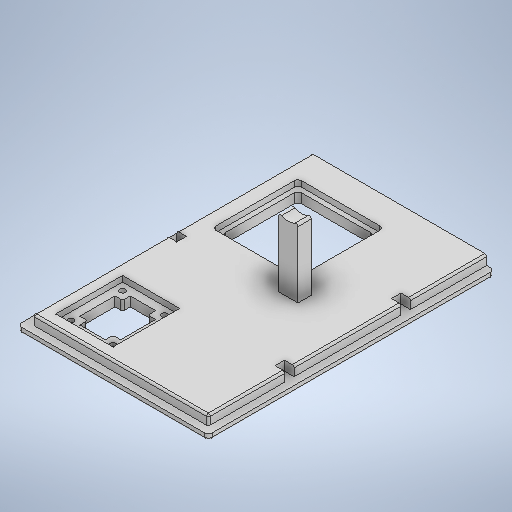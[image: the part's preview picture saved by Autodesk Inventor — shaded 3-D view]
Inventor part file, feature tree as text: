
AUTODESK INVENTOR PART (.ipt)
format: ipt  version: 2025 (Build 290162000, 162)  size: 964,608 bytes
history: native  units: mm
features: extrude x8, sketch x7, fillet x5, other x2
ambient origin geometry x8: Origin, YZ Plane, XZ Plane, XY Plane, X Axis, Y Axis, Z Axis, Center Point
bodies: Body1 (feature_tree)
feature tree (22):
  other  "ソリッド1"
  extrude  "底面"  Depth=100.0mm
  extrude  "溝"  Depth=150.0mm
  extrude  "支柱"  Depth=8.0mm TaperAngle=0.0deg
  extrude  "押し出し4"  Depth=30.0mm
  fillet  "フィレット1"  Radius=35.0mm
  extrude  "ケース用溝"  Depth=10.0mm
  fillet  "フィレット2"  Radius=3.0mm
  fillet  "フィレット3"  Radius=41.0mm
  extrude  "押し出し6"  Depth=39.0mm TaperAngle=0.0deg
  extrude  "ネジ穴"  Depth=13.0mm
  fillet  "フィレット4"  Radius=1.0mm
  extrude  "ナット穴"  Depth=45.0mm
  fillet  "フィレット5"  Radius=45.0mm
  other  "底面スケッチ"
  sketch  "スケッチ2"
  sketch  "スケッチ3"
  sketch  "スケッチ4"
  sketch  "スケッチ5"
  sketch  "スケッチ6"
  sketch  "スケッチ7"
  sketch  "スケッチ8"
